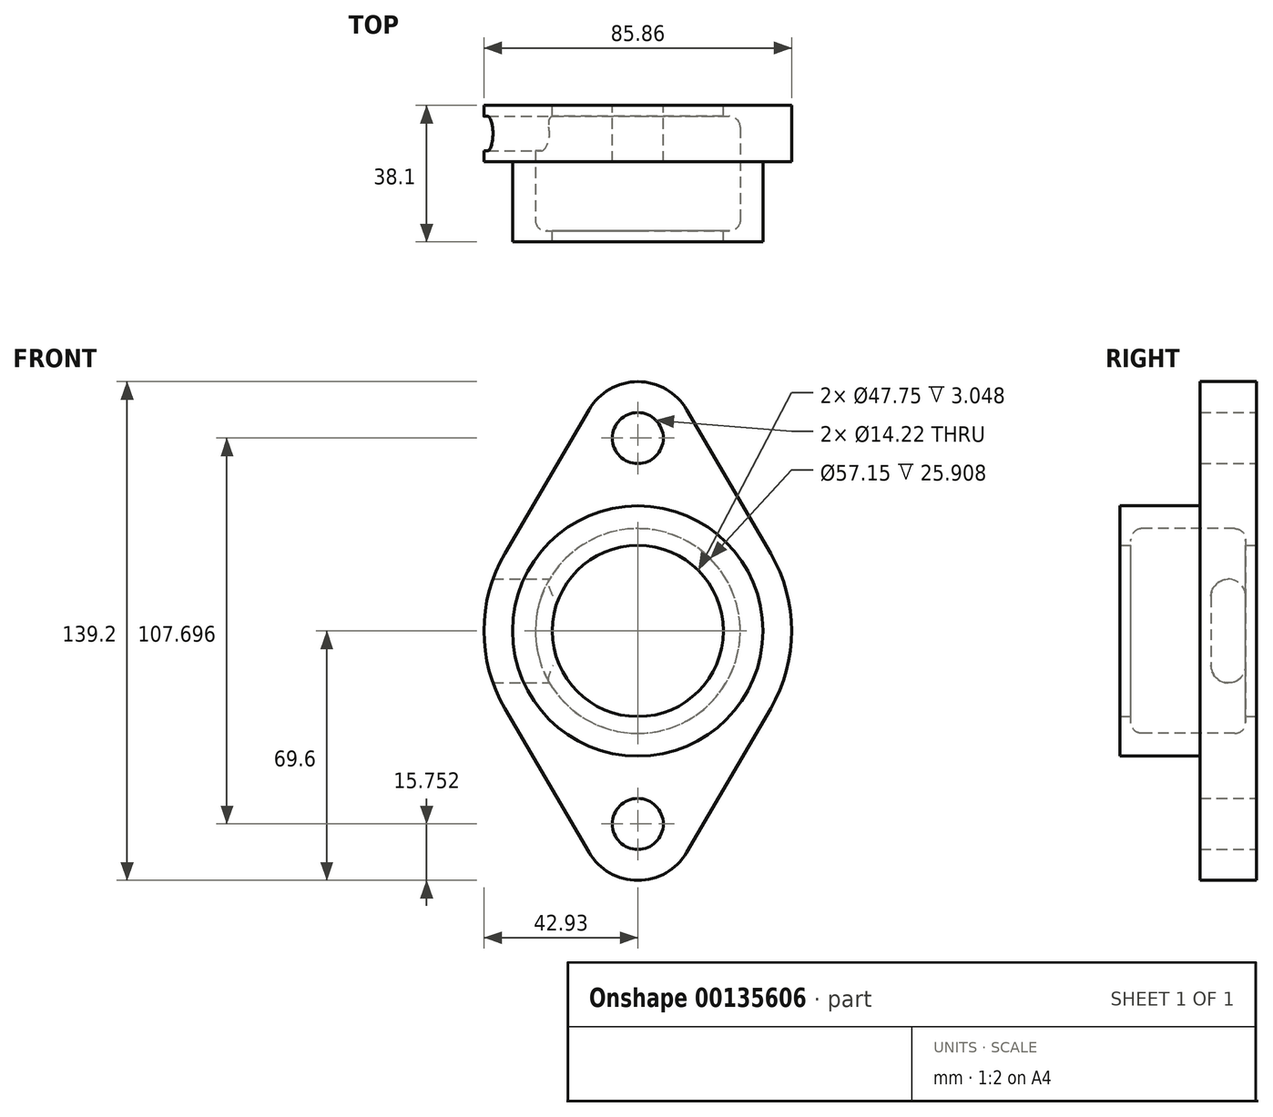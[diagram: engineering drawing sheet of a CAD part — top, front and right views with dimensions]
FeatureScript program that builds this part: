
annotation { "Feature Type Name" : "Feature", "Feature Type Description" : "" }
export const myFeature = defineFeature(function(context is Context, id is Id, definition is map)
    precondition{}
    {
        {
            var Q0;
            Q0=qCreatedBy(makeId("Front.planeOp"),FACE);
            var sketch = newSketch(context, id + "F0", { "sketchPlane" : qUnion([Q0])});
            skLineSegment(sketch, "E0", {"start": v(-37.06, 21.67) * mm, "end": v(-13.6, 61.8) * mm});
            skLineSegment(sketch, "E1", {"start": v(13.6, 61.8) * mm, "end": v(37.06, 21.67) * mm});
            skLineSegment(sketch, "E2", {"start": v(37.06, -21.67) * mm, "end": v(13.6, -61.8) * mm});
            skLineSegment(sketch, "E3", {"start": v(-13.6, -61.8) * mm, "end": v(-37.06, -21.67) * mm});
            skArc(sketch, "E4", {"start": v(-37.06, 21.67) * mm, "mid": v(-42.93, 0) * mm, "end": v(-37.06, -21.67) * mm});
            skArc(sketch, "E5", {"start": v(13.6, 61.8) * mm, "mid": v(0, 69.6) * mm, "end": v(-13.6, 61.8) * mm});
            skArc(sketch, "E6", {"start": v(37.06, -21.67) * mm, "mid": v(42.93, 0) * mm, "end": v(37.06, 21.67) * mm});
            skArc(sketch, "E7", {"start": v(-13.6, -61.8) * mm, "mid": v(0, -69.6) * mm, "end": v(13.6, -61.8) * mm});
            skCircle(sketch, "E8", {"center": v(0, 53.85) * mm, "radius": 7.11 * mm});
            skCircle(sketch, "E9", {"center": v(0, -53.85) * mm, "radius": 7.11 * mm});
            skCircle(sketch, "E10", {"center": v(0, 0) * mm, "radius": 23.88 * mm});
            skCircle(sketch, "E11", {"center": v(0, 0) * mm, "radius": 34.93 * mm});
            skCircle(sketch, "E12", {"center": v(0, 0) * mm, "radius": 28.58 * mm, "construction": true});
            skLineSegment(sketch, "E13", {"start": v(0, 0) * mm, "end": v(98.04, 0) * mm, "construction": true});
            skSolve(sketch);
        }
        {
            var Q0;
            Q0=makeQuery(id+"F0.imprint","IMPRINT",FACE,{"disambiguationData":[TD([[makeQuery(id+"F0.imprint","IMPRINT",EDGE,{"derivedFrom":sQuery(id+"F0.wireOp",EDGE,"E10")}),-1.0]])]});
            extrude(context, id + "F1", {"entities" : qUnion([Q0]), "depth" : 38.1 * mm});
        }
        {
            var Q0;
            Q0=makeQuery(id+"F0.imprint","IMPRINT",FACE,{"disambiguationData":[TD([[makeQuery(id+"F0.imprint","IMPRINT",EDGE,{"derivedFrom":sQuery(id+"F0.wireOp",EDGE,"E0")}),-1.0]])]});
            extrude(context, id + "F2", {"entities" : qUnion([Q0]), "operationType" : NewBodyOperationType.ADD, "depth" : 15.75 * mm});
        }
        {
            var Q0;
            Q0=qCreatedBy(makeId("Right.planeOp"),FACE);
            var sketch = newSketch(context, id + "F3", { "sketchPlane" : qUnion([Q0])});
            skLineSegment(sketch, "E14", {"start": v(0, 0) * mm, "end": v(-7.87, 0) * mm, "construction": true});
            skLineSegment(sketch, "E15", {"start": v(-7.87, 0) * mm, "end": v(-38.1, 0) * mm, "construction": true});
            skLineSegment(sketch, "E16", {"start": v(-7.87, 0) * mm, "end": v(-7.87, 9.65) * mm, "construction": true});
            skLineSegment(sketch, "E17", {"start": v(-7.87, 0) * mm, "end": v(-7.87, -9.65) * mm, "construction": true});
            skCircle(sketch, "E18", {"center": v(-7.87, 9.65) * mm, "radius": 4.83 * mm});
            skCircle(sketch, "E19", {"center": v(-7.87, -9.65) * mm, "radius": 4.83 * mm});
            skLineSegment(sketch, "E20", {"start": v(-12.7, 9.65) * mm, "end": v(-12.7, -9.65) * mm});
            skLineSegment(sketch, "E21", {"start": v(-3.05, 9.65) * mm, "end": v(-3.05, -9.65) * mm});
            skSolve(sketch);
        }
        {
            var Q0;
            Q0 = qSketchRegion(id + "F3", true);
            extrude(context, id + "F4", {"entities" : qUnion([Q0]), "operationType" : NewBodyOperationType.REMOVE, "endBound" : BoundingType.THROUGH_ALL, "oppositeDirection" : true, "depth" : 25.4 * mm});
        }
        {
            var Q0;
            Q0=qCreatedBy(makeId("Top.planeOp"),FACE);
            var sketch = newSketch(context, id + "F5", { "sketchPlane" : qUnion([Q0])});
            skLineSegment(sketch, "E22.bottom", {"start": v(0, -3.05) * mm, "end": v(25.53, -3.05) * mm});
            skLineSegment(sketch, "E22.top", {"start": v(0, -35.05) * mm, "end": v(25.53, -35.05) * mm});
            skLineSegment(sketch, "E22.right", {"start": v(28.58, -6.1) * mm, "end": v(28.58, -32) * mm});
            skArc(sketch, "E23", {"start": v(28.58, -6.1) * mm, "mid": v(27.68, -3.94) * mm, "end": v(25.53, -3.05) * mm});
            skArc(sketch, "E24", {"start": v(25.53, -35.05) * mm, "mid": v(27.68, -34.16) * mm, "end": v(28.58, -32) * mm});
            skLineSegment(sketch, "E25", {"start": v(0, 10.6) * mm, "end": v(0, -46.72) * mm, "construction": true});
            skLineSegment(sketch, "E26", {"start": v(0, -3.05) * mm, "end": v(0, -35.05) * mm});
            skSolve(sketch);
        }
        {
            var Q0;
            Q0 = qSketchRegion(id + "F5", true);
            var Q1;
            Q1=sQuery(id+"F5.wireOp",EDGE,"E25");
            revolve(context, id + "F6", {"operationType" : NewBodyOperationType.REMOVE, "entities" : qUnion([Q0]), "axis" : qUnion([Q1]), "revolveType" : RevolveType.FULL, "oppositeDirection" : true});
        }
    });
